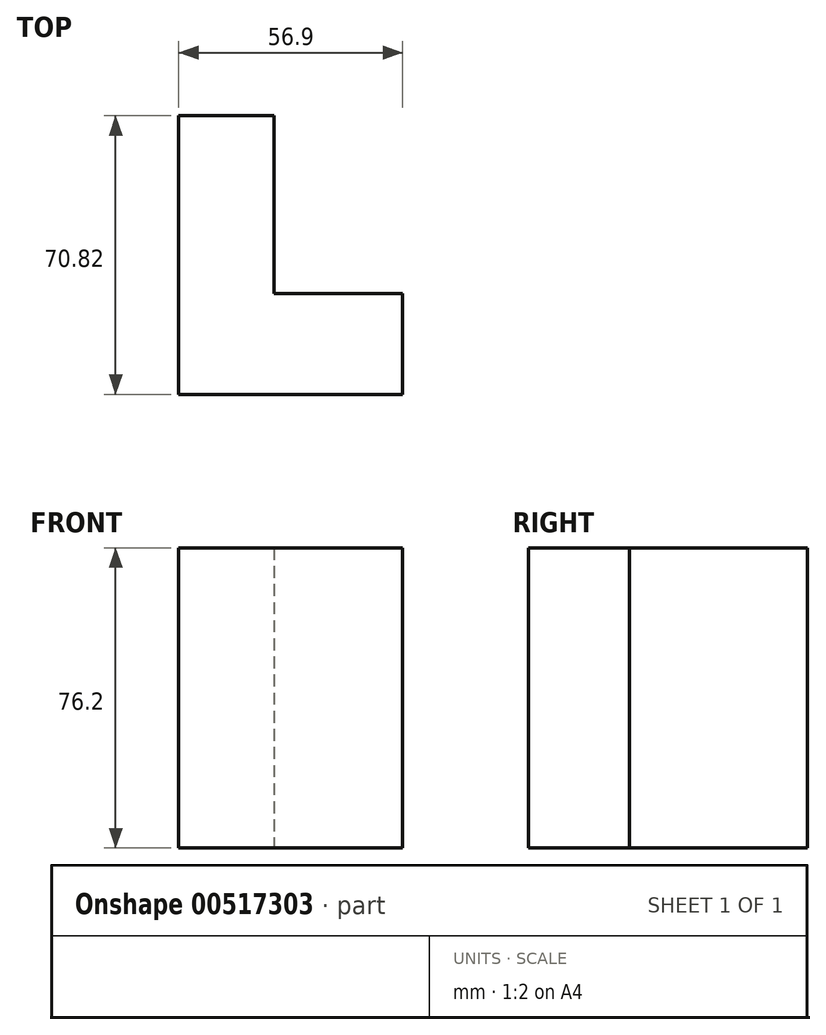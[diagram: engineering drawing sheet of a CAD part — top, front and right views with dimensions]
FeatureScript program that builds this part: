
annotation { "Feature Type Name" : "Feature", "Feature Type Description" : "" }
export const myFeature = defineFeature(function(context is Context, id is Id, definition is map)
    precondition{}
    {
        {
            var Q0;
            Q0=qCreatedBy(makeId("Top.planeOp"),FACE);
            var sketch = newSketch(context, id + "F0", { "sketchPlane" : qUnion([Q0])});
            skLineSegment(sketch, "E0", {"start": v(0, 0) * mm, "end": v(32.63, 0) * mm});
            skLineSegment(sketch, "E1", {"start": v(32.63, 0) * mm, "end": v(32.63, -25.66) * mm});
            skLineSegment(sketch, "E2", {"start": v(32.63, -25.66) * mm, "end": v(-24.27, -25.66) * mm});
            skLineSegment(sketch, "E3", {"start": v(-24.27, -25.66) * mm, "end": v(-24.27, 45.16) * mm});
            skLineSegment(sketch, "E4", {"start": v(-24.27, 45.16) * mm, "end": v(0, 45.16) * mm});
            skLineSegment(sketch, "E5", {"start": v(0, 45.16) * mm, "end": v(0, 0) * mm});
            skSolve(sketch);
        }
        {
            var Q0;
            Q0 = qSketchRegion(id + "F0", true);
            extrude(context, id + "F1", {"entities" : qUnion([Q0]), "depth" : 76.2 * mm, "offsetDistance" : 25.4 * mm});
        }
    });
